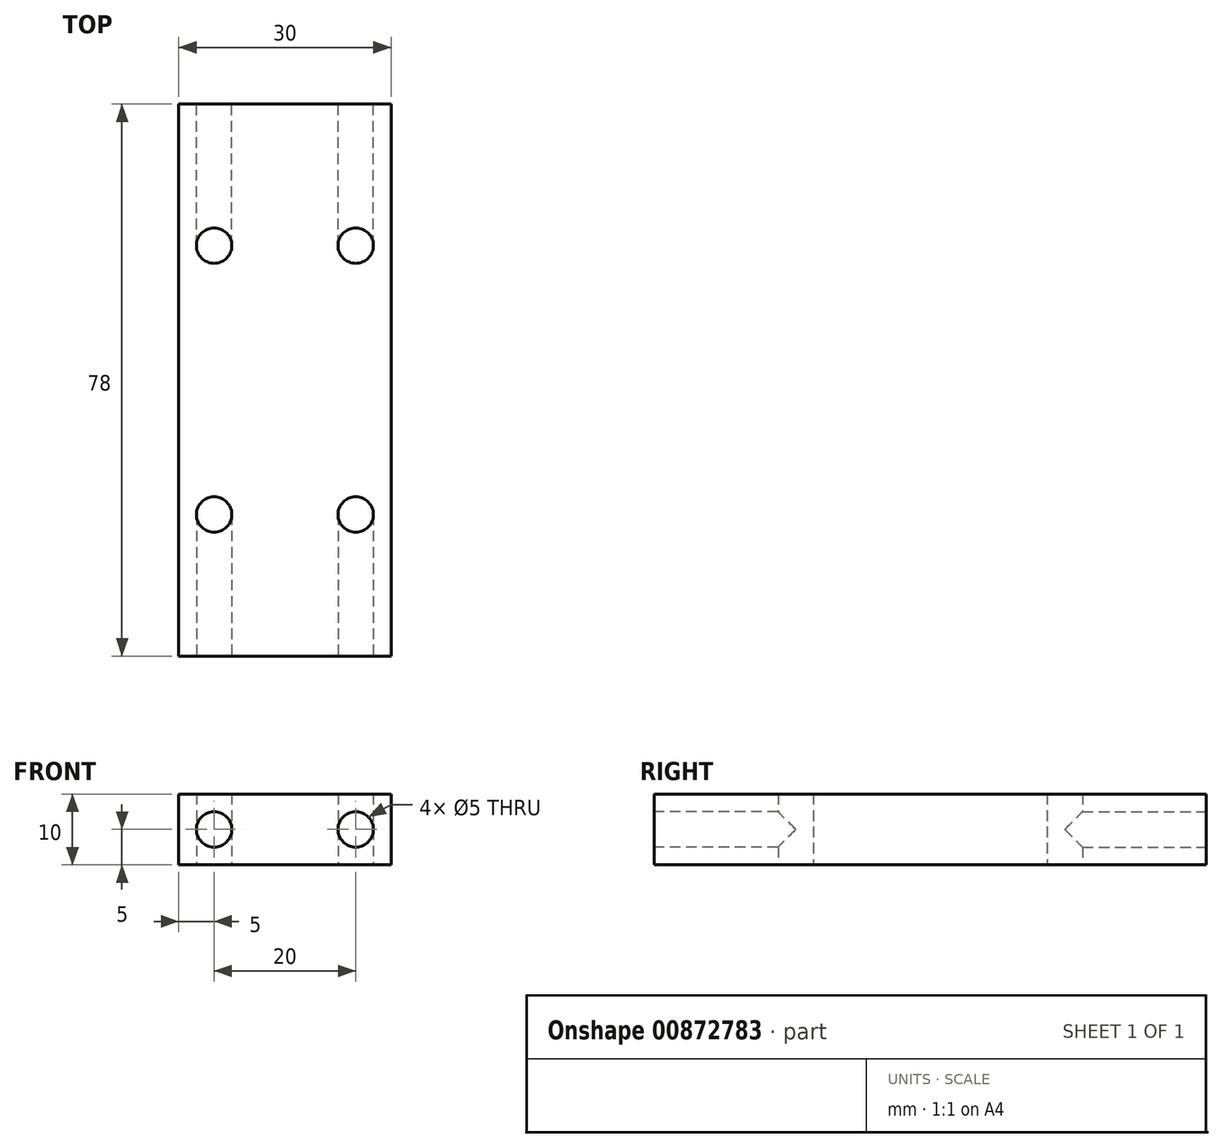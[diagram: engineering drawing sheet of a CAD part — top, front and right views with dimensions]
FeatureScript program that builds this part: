
annotation { "Feature Type Name" : "Feature", "Feature Type Description" : "" }
export const myFeature = defineFeature(function(context is Context, id is Id, definition is map)
    precondition{}
    {
        {
            var Q0;
            Q0=qCreatedBy(makeId("Top.planeOp"),FACE);
            var sketch = newSketch(context, id + "F0", { "sketchPlane" : qUnion([Q0])});
            skLineSegment(sketch, "E0.bottom", {"start": v(15, 39) * mm, "end": v(-15, 39) * mm});
            skLineSegment(sketch, "E0.top", {"start": v(15, -39) * mm, "end": v(-15, -39) * mm});
            skLineSegment(sketch, "E0.left", {"start": v(15, 39) * mm, "end": v(15, -39) * mm});
            skLineSegment(sketch, "E0.right", {"start": v(-15, 39) * mm, "end": v(-15, -39) * mm});
            skPoint(sketch, "E0.middle", {"position": v(0, 0) * mm});
            skPoint(sketch, "E1.centerSnap0", {"position": v(15, 0) * mm});
            skPoint(sketch, "E2.centerSnap0", {"position": v(-15, 0) * mm});
            skPoint(sketch, "E3.centerSnap0", {"position": v(0, -39) * mm});
            skPoint(sketch, "E4.centerSnap0", {"position": v(0, 39) * mm});
            skCircle(sketch, "E5", {"center": v(-10, -19) * mm, "radius": 2.5 * mm});
            skCircle(sketch, "E6", {"center": v(-10, 19) * mm, "radius": 2.5 * mm});
            skCircle(sketch, "E7", {"center": v(10, -19) * mm, "radius": 2.5 * mm});
            skCircle(sketch, "E8", {"center": v(10, 19) * mm, "radius": 2.5 * mm});
            skSolve(sketch);
        }
        {
            var Q0;
            Q0=makeQuery(id+"F0.imprint","IMPRINT",FACE,{"disambiguationData":[TD([[makeQuery(id+"F0.imprint","IMPRINT",EDGE,{"derivedFrom":sQuery(id+"F0.wireOp",EDGE,"E0.bottom")}),1.0]])]});
            extrude(context, id + "F1", {"entities" : qUnion([Q0]), "depth" : 10 * mm, "offsetDistance" : 25 * mm});
        }
        {
            var Q0;
            Q0=makeQuery(id+"F1.opExtrude","SWEPT_FACE",FACE,{"disambiguationData":[OSD([sQuery(id+"F0.wireOp",EDGE,"E0.top")])]});
            var sketch = newSketch(context, id + "F2", { "sketchPlane" : qUnion([Q0])});
            skCircle(sketch, "E9", {"center": v(-10, 5) * mm, "radius": 2.5 * mm});
            skPoint(sketch, "E9.centerSnap0", {"position": v(-15, 5) * mm});
            skCircle(sketch, "E10", {"center": v(10, 5) * mm, "radius": 2.5 * mm});
            skPoint(sketch, "E10.centerSnap0", {"position": v(15, 5) * mm});
            skSolve(sketch);
        }
        {
            var Q0;
            Q0=qSketchRegion(id+"F2",true);
            extrude(context, id + "F3", {"entities" : qUnion([Q0]), "operationType" : NewBodyOperationType.REMOVE, "oppositeDirection" : true, "depth" : 20 * mm, "offsetDistance" : 25 * mm});
        }
        {
            var Q0;
            Q0=makeQuery(id+"F1.opExtrude","SWEPT_FACE",FACE,{"disambiguationData":[OSD([sQuery(id+"F0.wireOp",EDGE,"E0.bottom")])]});
            var sketch = newSketch(context, id + "F4", { "sketchPlane" : qUnion([Q0])});
            skCircle(sketch, "E11", {"center": v(-10, 5) * mm, "radius": 2.5 * mm});
            skPoint(sketch, "E11.centerSnap0", {"position": v(-15, 5) * mm});
            skCircle(sketch, "E12", {"center": v(10, 5) * mm, "radius": 2.5 * mm});
            skPoint(sketch, "E12.centerSnap0", {"position": v(15, 5) * mm});
            skSolve(sketch);
        }
        {
            var Q0;
            Q0=qSketchRegion(id+"F4",true);
            extrude(context, id + "F5", {"entities" : qUnion([Q0]), "operationType" : NewBodyOperationType.REMOVE, "oppositeDirection" : true, "depth" : 20 * mm, "offsetDistance" : 25 * mm});
        }
    });
